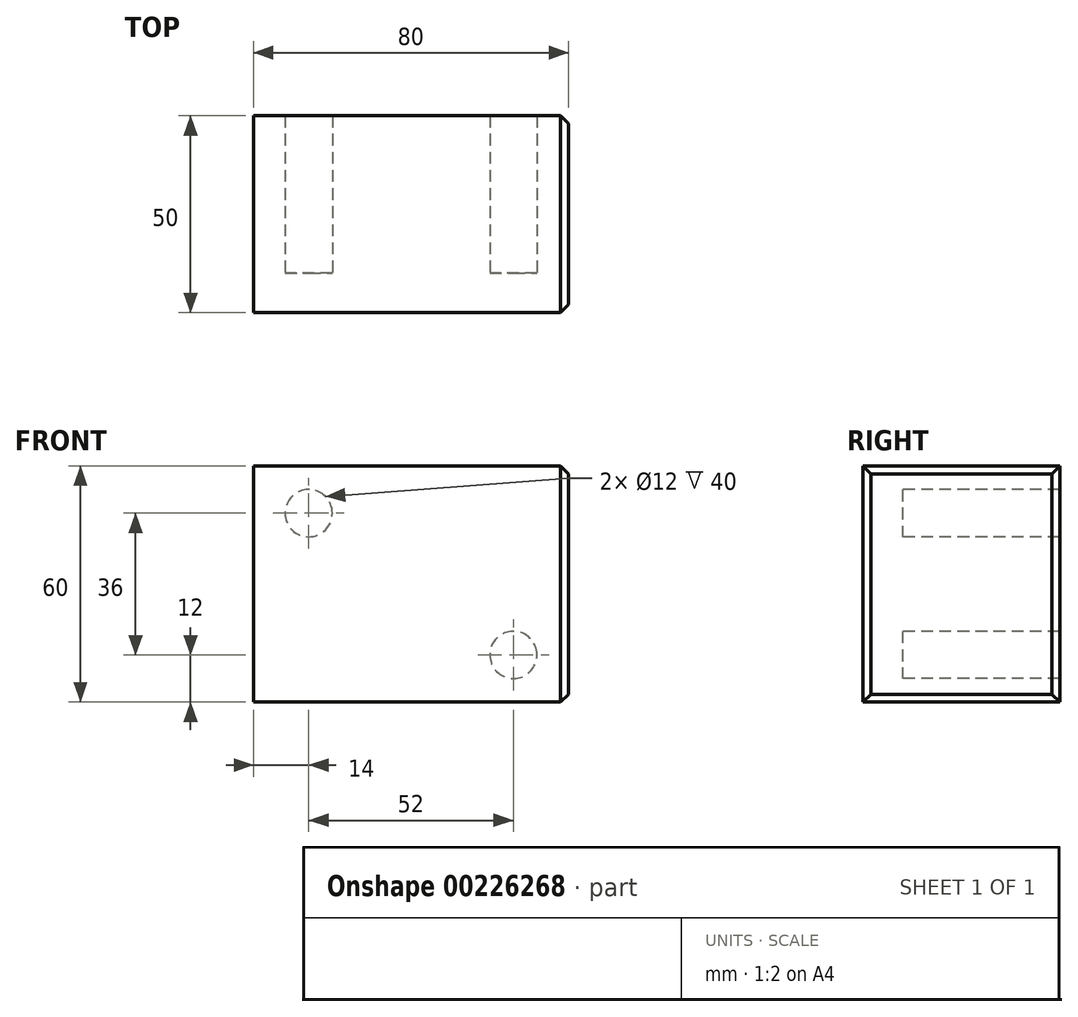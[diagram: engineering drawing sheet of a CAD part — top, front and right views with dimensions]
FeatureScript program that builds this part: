
annotation { "Feature Type Name" : "Feature", "Feature Type Description" : "" }
export const myFeature = defineFeature(function(context is Context, id is Id, definition is map)
    precondition{}
    {
        {
            var Q0;
            Q0=qCreatedBy(makeId("Front.planeOp"),FACE);
            var sketch = newSketch(context, id + "F0", { "sketchPlane" : qUnion([Q0])});
            skLineSegment(sketch, "E0.bottom", {"start": v(-40, 30) * mm, "end": v(40, 30) * mm});
            skLineSegment(sketch, "E0.top", {"start": v(-40, -30) * mm, "end": v(40, -30) * mm});
            skLineSegment(sketch, "E0.left", {"start": v(-40, 30) * mm, "end": v(-40, -30) * mm});
            skLineSegment(sketch, "E0.right", {"start": v(40, 30) * mm, "end": v(40, -30) * mm});
            skPoint(sketch, "E0.middle", {"position": v(0, 0) * mm});
            skSolve(sketch);
        }
        {
            var Q0;
            Q0=makeQuery(id+"F0.imprint","IMPRINT",FACE,{"disambiguationData":[TD([[makeQuery(id+"F0.imprint","IMPRINT",EDGE,{"derivedFrom":sQuery(id+"F0.wireOp",EDGE,"E0.bottom")}),-1.0]])]});
            extrude(context, id + "F1", {"entities" : qUnion([Q0]), "depth" : 10 * mm});
        }
        {
            var Q0;
            Q0=makeQuery(id+"F1.opExtrude","CAP_FACE",FACE,{"disambiguationData":[OSD([sQuery(id+"F0.wireOp",EDGE,"E0.bottom"),sQuery(id+"F0.wireOp",EDGE,"E0.top"),sQuery(id+"F0.wireOp",EDGE,"E0.left"),sQuery(id+"F0.wireOp",EDGE,"E0.right")])],"isStart":true});
            var sketch = newSketch(context, id + "F2", { "sketchPlane" : qUnion([Q0])});
            skCircle(sketch, "E1", {"center": v(26, -18) * mm, "radius": 6 * mm});
            skCircle(sketch, "E2.MirrorC", {"center": v(26, 18) * mm, "radius": 6 * mm});
            skCircle(sketch, "E3.MirrorC", {"center": v(-26, 18) * mm, "radius": 6 * mm});
            skCircle(sketch, "E4.MirrorC", {"center": v(-26, -18) * mm, "radius": 6 * mm});
            skSolve(sketch);
        }
        {
            var Q0;
            Q0=makeQuery(id+"F2.imprint","IMPRINT",FACE,{"disambiguationData":[TD([[makeQuery(id+"F2.imprint","IMPRINT",EDGE,{"derivedFrom":sQuery(id+"F2.wireOp",EDGE,"E2.MirrorC")}),-1.0]])]});
            var Q1;
            Q1=makeQuery(id+"F2.imprint","IMPRINT",FACE,{"disambiguationData":[TD([[makeQuery(id+"F2.imprint","IMPRINT",EDGE,{"derivedFrom":sQuery(id+"F2.wireOp",EDGE,"E1")}),1.0]])]});
            var Q2;
            Q2=makeQuery(id+"F2.imprint","IMPRINT",FACE,{"disambiguationData":[TD([[makeQuery(id+"F2.imprint","IMPRINT",EDGE,{"derivedFrom":sQuery(id+"F2.wireOp",EDGE,"E4.MirrorC")}),-1.0]])]});
            var Q3;
            Q3=makeQuery(id+"F2.imprint","IMPRINT",FACE,{"disambiguationData":[TD([[makeQuery(id+"F2.imprint","IMPRINT",EDGE,{"derivedFrom":sQuery(id+"F2.wireOp",EDGE,"E3.MirrorC")}),1.0]])]});
            extrude(context, id + "F3", {"entities" : qUnion([Q0, Q1, Q2, Q3]), "operationType" : NewBodyOperationType.ADD, "depth" : 40 * mm});
        }
        {
            var Q0;
            Q0=makeQuery(id+"F1.opExtrude","SWEPT_FACE",FACE,{"disambiguationData":[OSD([sQuery(id+"F0.wireOp",EDGE,"E0.right")])]});
            chamfer(context, id + "F4", {"entities" : qUnion([Q0]), "width" : 2 * mm, "tangentPropagation" : true});
        }
    });
